# Revit family: 9517b277-2e63-4364-996c-b4e9128951dc
name_source: partatom
category: Двери
revit_build: Autodesk Revit 2017 (Build: 20170419_0315(x64)
units: mm (PartAtom-declared; Revit-internal decimal feet)

## family parameters
Всегда вертикально = Да
Заголовок OmniClass = Doors
Номер OmniClass = 23.30.10.00
Общий = Нет
Основа = Стена
При загрузке вырезать с полостями = Нет
Точка расчета площади = Нет

## types (3) — shared parameters
Аналитическая конструкция = <Нет>
Высота = 2100 мм
Высота полотна двери = 1990 мм
Зазор = 10 мм
Замыкание стены = По основе
Материал коробки = Дерево
Материал полотна двери = Дерево
Материал ручки двери = Металл крашенный темно-серый
Материал стекла = Стекло
О_URLСтраницыИзделия = http://bimacad.pro
О_Изображение = <Нет>
О_Материал = <По категории>
Примерная высота = 2100 мм
Р_Высота = 2100 мм
Р_Толщина = 100 мм
Смещение ручки по X = 100 мм
Смещение ручки по Z = 1000 мм
Толщина = 100 мм
Толщина коробки = 100 мм
Толщина полотна двери = 80 мм
Угол открывания = 30.00°
Функция = Внутренние слои
Ширина коробки = 100 мм
zero-valued in all types: Стоимость изделия

## per-type parameters (varying)
| type | Левое открывание | Полотно двери | Правое открывание | Примерная ширина | Р_Длина | Р_Ширина | Ширина |
| ДВ-1 (21-10) | Нет | 101_ПолотноДвериСплошное | Да | 1000 мм | 1000 мм | 1000 мм | 1000 мм |
| ДВ-2 (21-10) Л | Да | 101_ПолотноДвериСплошное | Нет | 1000 мм | 1000 мм | 1000 мм | 1000 мм |
| ДВ-3 (21-12) | Нет | 101_ПолотноДвериСоСтеклом | Да | 1200 мм | 1200 мм | 1200 мм | 1200 мм |
